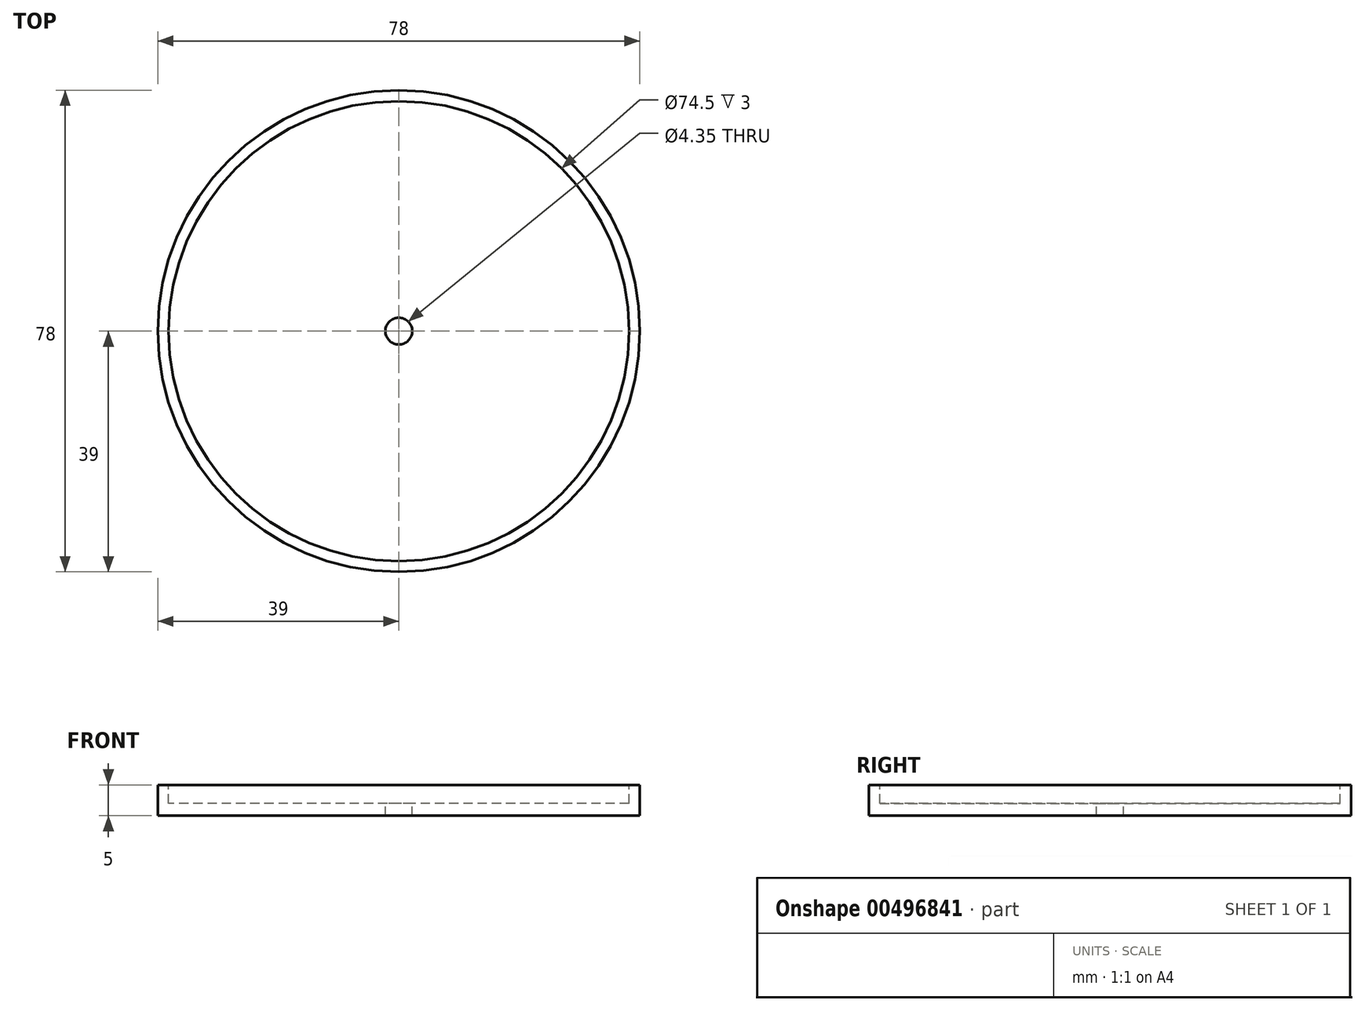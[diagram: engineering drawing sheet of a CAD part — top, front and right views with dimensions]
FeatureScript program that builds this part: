
annotation { "Feature Type Name" : "Feature", "Feature Type Description" : "" }
export const myFeature = defineFeature(function(context is Context, id is Id, definition is map)
    precondition{}
    {
        {
            var Q0;
            Q0=qCreatedBy(makeId("Top.planeOp"),FACE);
            var sketch = newSketch(context, id + "F0", { "sketchPlane" : qUnion([Q0])});
            skCircle(sketch, "E0", {"center": v(0, 0) * mm, "radius": 39 * mm});
            skSolve(sketch);
        }
        {
            var Q0;
            Q0=makeQuery(id+"F0.imprint","IMPRINT",FACE,{"disambiguationData":[TD([[makeQuery(id+"F0.imprint","IMPRINT",EDGE,{"derivedFrom":sQuery(id+"F0.wireOp",EDGE,"E0")}),1.0]])]});
            extrude(context, id + "F1", {"entities" : qUnion([Q0]), "depth" : 5 * mm});
        }
        {
            var Q0;
            Q0=makeQuery(id+"F1.opExtrude","CAP_FACE",FACE,{"disambiguationData":[OSD([sQuery(id+"F0.wireOp",EDGE,"E0")])],"isStart":false});
            var sketch = newSketch(context, id + "F2", { "sketchPlane" : qUnion([Q0])});
            skCircle(sketch, "E1", {"center": v(0, 0) * mm, "radius": 37.25 * mm});
            skSolve(sketch);
        }
        {
            var Q0;
            Q0=makeQuery(id+"F2.imprint","IMPRINT",FACE,{"disambiguationData":[TD([[makeQuery(id+"F2.imprint","IMPRINT",EDGE,{"derivedFrom":sQuery(id+"F2.wireOp",EDGE,"E1")}),1.0]])]});
            extrude(context, id + "F3", {"entities" : qUnion([Q0]), "operationType" : NewBodyOperationType.REMOVE, "oppositeDirection" : true, "depth" : 3 * mm});
        }
        {
            var Q0;
            Q0=makeQuery(id+"F3.boolean.opBoolean","COPY",FACE,{"derivedFrom":makeQuery(id+"F3.opExtrude","CAP_FACE",FACE,{"disambiguationData":[OSD([sQuery(id+"F2.wireOp",EDGE,"E1")])],"isStart":false})});
            var sketch = newSketch(context, id + "F4", { "sketchPlane" : qUnion([Q0])});
            skCircle(sketch, "E2", {"center": v(0, 0) * mm, "radius": 2.17 * mm});
            skSolve(sketch);
        }
        {
            var Q0;
            Q0=makeQuery(id+"F4.imprint","IMPRINT",FACE,{"disambiguationData":[TD([[makeQuery(id+"F4.imprint","IMPRINT",EDGE,{"derivedFrom":sQuery(id+"F4.wireOp",EDGE,"E2")}),1.0]])]});
            extrude(context, id + "F5", {"entities" : qUnion([Q0]), "operationType" : NewBodyOperationType.REMOVE, "oppositeDirection" : true, "depth" : 3 * mm});
        }
    });
